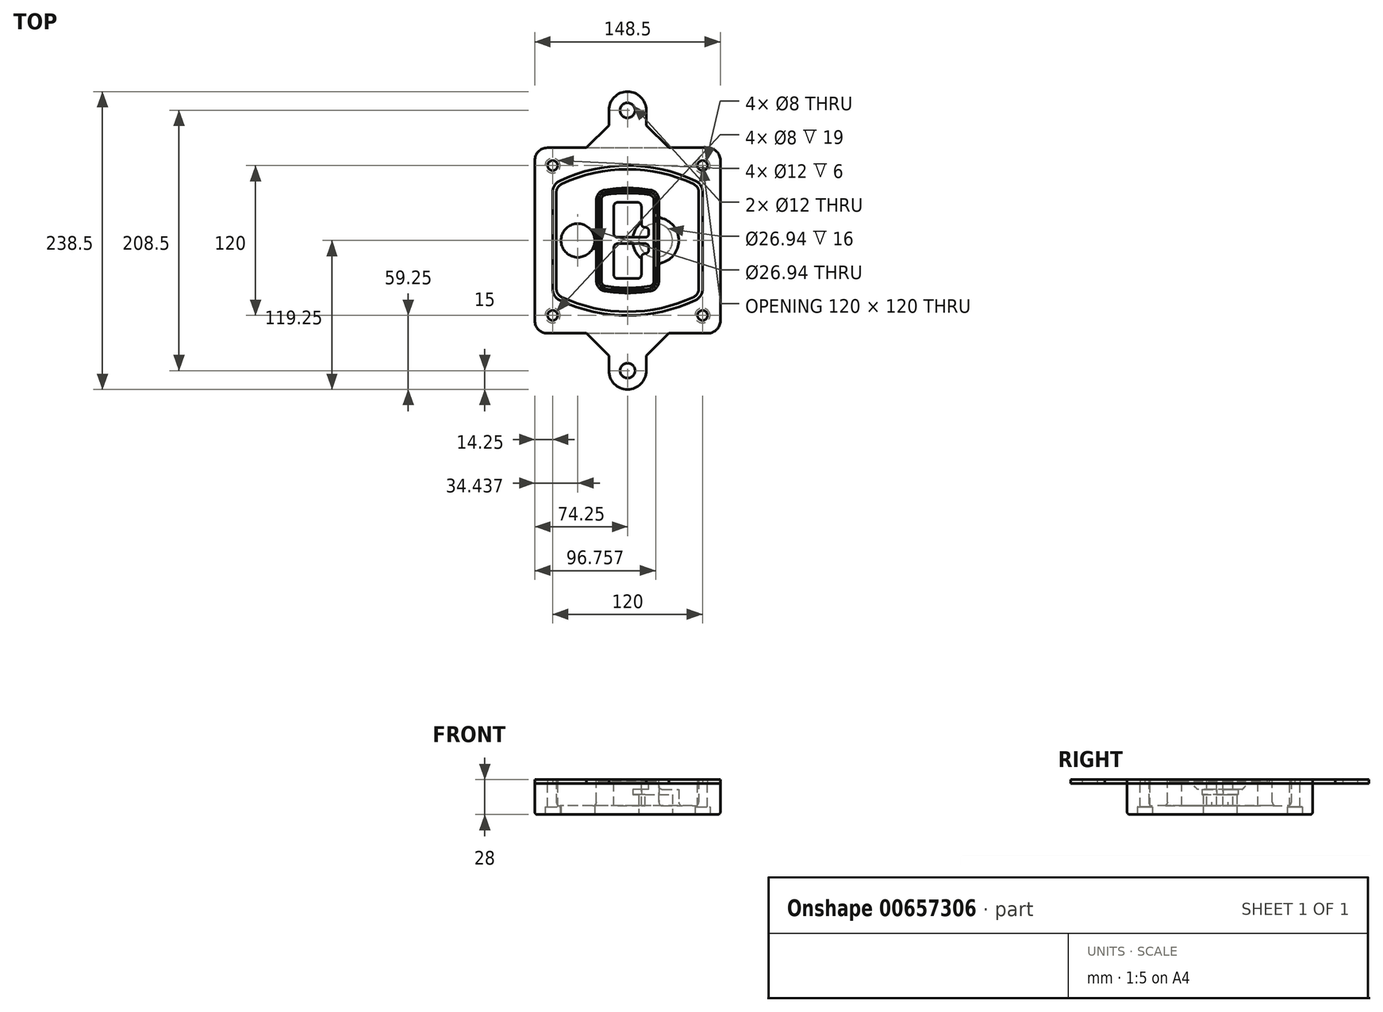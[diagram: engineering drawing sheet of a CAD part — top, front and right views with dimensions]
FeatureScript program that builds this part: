
annotation { "Feature Type Name" : "Feature", "Feature Type Description" : "" }
export const myFeature = defineFeature(function(context is Context, id is Id, definition is map)
    precondition{}
    {
        {
            var Q0;
            Q0=qCreatedBy(makeId("Top.planeOp"),FACE);
            var sketch = newSketch(context, id + "F0", { "sketchPlane" : qUnion([Q0])});
            skPoint(sketch, "E0.rect.middle", {"position": v(0, 0) * mm});
            skLineSegment(sketch, "E1.bottom", {"start": v(-64.25, -74.25) * mm, "end": v(64.25, -74.25) * mm});
            skLineSegment(sketch, "E1.top", {"start": v(-64.25, 74.25) * mm, "end": v(64.25, 74.25) * mm});
            skLineSegment(sketch, "E1.left", {"start": v(-74.25, -64.25) * mm, "end": v(-74.25, 64.25) * mm});
            skLineSegment(sketch, "E1.right", {"start": v(74.25, -64.25) * mm, "end": v(74.25, 64.25) * mm});
            skLineSegment(sketch, "E2", {"start": v(-74.25, 74.25) * mm, "end": v(74.25, -74.25) * mm, "construction": true});
            skLineSegment(sketch, "E3", {"start": v(74.25, 74.25) * mm, "end": v(-74.25, -74.25) * mm, "construction": true});
            skCircle(sketch, "E4", {"center": v(-60, 60) * mm, "radius": 4 * mm});
            skCircle(sketch, "E5", {"center": v(60, 60) * mm, "radius": 4 * mm});
            skCircle(sketch, "E6", {"center": v(60, -60) * mm, "radius": 4 * mm});
            skCircle(sketch, "E7", {"center": v(-60, -60) * mm, "radius": 4 * mm});
            skLineSegment(sketch, "E8", {"start": v(-60, 60) * mm, "end": v(60, 60) * mm, "construction": true});
            skLineSegment(sketch, "E9", {"start": v(60, 60) * mm, "end": v(60, -60) * mm, "construction": true});
            skLineSegment(sketch, "E10", {"start": v(60, -60) * mm, "end": v(-60, -60) * mm, "construction": true});
            skLineSegment(sketch, "E11", {"start": v(-60, -60) * mm, "end": v(-60, 60) * mm, "construction": true});
            skLineSegment(sketch, "E12", {"start": v(-60, 38.83) * mm, "end": v(-60, -38.83) * mm});
            skLineSegment(sketch, "E13", {"start": v(60, 38.83) * mm, "end": v(60, -38.83) * mm});
            skArc(sketch, "E14", {"start": v(54.26, 47.88) * mm, "mid": v(0, 60) * mm, "end": v(-54.26, 47.88) * mm});
            skArc(sketch, "E15", {"start": v(-54.26, -47.88) * mm, "mid": v(0, -60) * mm, "end": v(54.26, -47.88) * mm});
            skLineSegment(sketch, "E16", {"start": v(-60, 0) * mm, "end": v(60, 0) * mm, "construction": true});
            skPoint(sketch, "E17.visualSharp", {"position": v(-60, -45) * mm});
            skArc(sketch, "E17.filletArc", {"start": v(-60, -38.83) * mm, "mid": v(-58.44, -44.2) * mm, "end": v(-54.26, -47.88) * mm});
            skPoint(sketch, "E18.visualSharp", {"position": v(-60, 45) * mm});
            skArc(sketch, "E18.filletArc", {"start": v(-54.26, 47.88) * mm, "mid": v(-58.44, 44.2) * mm, "end": v(-60, 38.83) * mm});
            skPoint(sketch, "E19.visualSharp", {"position": v(60, 45) * mm});
            skArc(sketch, "E19.filletArc", {"start": v(60, 38.83) * mm, "mid": v(58.44, 44.2) * mm, "end": v(54.26, 47.88) * mm});
            skPoint(sketch, "E20.visualSharp", {"position": v(60, -45) * mm});
            skArc(sketch, "E20.filletArc", {"start": v(54.26, -47.88) * mm, "mid": v(58.44, -44.2) * mm, "end": v(60, -38.83) * mm});
            skPoint(sketch, "E21.visualSharp", {"position": v(-74.25, 74.25) * mm});
            skArc(sketch, "E21.filletArc", {"start": v(-64.25, 74.25) * mm, "mid": v(-71.32, 71.32) * mm, "end": v(-74.25, 64.25) * mm});
            skPoint(sketch, "E22.visualSharp", {"position": v(74.25, 74.25) * mm});
            skArc(sketch, "E22.filletArc", {"start": v(74.25, 64.25) * mm, "mid": v(71.32, 71.32) * mm, "end": v(64.25, 74.25) * mm});
            skPoint(sketch, "E23.visualSharp", {"position": v(74.25, -74.25) * mm});
            skArc(sketch, "E23.filletArc", {"start": v(64.25, -74.25) * mm, "mid": v(71.32, -71.32) * mm, "end": v(74.25, -64.25) * mm});
            skPoint(sketch, "E24.visualSharp", {"position": v(-74.25, -74.25) * mm});
            skArc(sketch, "E24.filletArc", {"start": v(-74.25, -64.25) * mm, "mid": v(-71.32, -71.32) * mm, "end": v(-64.25, -74.25) * mm});
            skArc(sketch, "E25.0", {"start": v(57, 38.83) * mm, "mid": v(55.9, 42.58) * mm, "end": v(52.98, 45.17) * mm});
            skLineSegment(sketch, "E25.1", {"start": v(57, 38.83) * mm, "end": v(57, -38.83) * mm});
            skArc(sketch, "E25.2", {"start": v(52.98, -45.17) * mm, "mid": v(55.9, -42.58) * mm, "end": v(57, -38.83) * mm});
            skArc(sketch, "E25.3", {"start": v(-52.98, -45.17) * mm, "mid": v(0, -57) * mm, "end": v(52.98, -45.17) * mm});
            skArc(sketch, "E25.4", {"start": v(-57, -38.83) * mm, "mid": v(-55.9, -42.58) * mm, "end": v(-52.98, -45.17) * mm});
            skArc(sketch, "E25.5", {"start": v(52.98, 45.17) * mm, "mid": v(0, 57) * mm, "end": v(-52.98, 45.17) * mm});
            skLineSegment(sketch, "E25.6", {"start": v(-57, 38.83) * mm, "end": v(-57, -38.83) * mm});
            skArc(sketch, "E25.7", {"start": v(-52.98, 45.17) * mm, "mid": v(-55.9, 42.58) * mm, "end": v(-57, 38.83) * mm});
            skArc(sketch, "E26.0", {"start": v(-55.96, 51.5) * mm, "mid": v(-61.82, 46.33) * mm, "end": v(-64, 38.83) * mm});
            skArc(sketch, "E26.1", {"start": v(55.96, 51.5) * mm, "mid": v(0, 64) * mm, "end": v(-55.96, 51.5) * mm});
            skArc(sketch, "E26.2", {"start": v(64, 38.83) * mm, "mid": v(61.82, 46.33) * mm, "end": v(55.96, 51.5) * mm});
            skLineSegment(sketch, "E26.3", {"start": v(64, 38.83) * mm, "end": v(64, -38.83) * mm});
            skArc(sketch, "E26.4", {"start": v(55.96, -51.5) * mm, "mid": v(61.82, -46.33) * mm, "end": v(64, -38.83) * mm});
            skLineSegment(sketch, "E26.5", {"start": v(-64, 38.83) * mm, "end": v(-64, -38.83) * mm});
            skArc(sketch, "E26.6", {"start": v(-55.96, -51.5) * mm, "mid": v(0, -64) * mm, "end": v(55.96, -51.5) * mm});
            skArc(sketch, "E26.7", {"start": v(-64, -38.83) * mm, "mid": v(-61.82, -46.33) * mm, "end": v(-55.96, -51.5) * mm});
            skLineSegment(sketch, "E27", {"start": v(0, 74.25) * mm, "end": v(0, 104.25) * mm});
            skCircle(sketch, "E28", {"center": v(0, 104.25) * mm, "radius": 6 * mm});
            skArc(sketch, "E29", {"start": v(-15, 104.25) * mm, "mid": v(0, 119.25) * mm, "end": v(15, 104.25) * mm});
            skLineSegment(sketch, "E30", {"start": v(-15, 104.25) * mm, "end": v(-15, 92.25) * mm});
            skLineSegment(sketch, "E31", {"start": v(15, 104.25) * mm, "end": v(15, 92.25) * mm});
            skLineSegment(sketch, "E32", {"start": v(-15, 92.25) * mm, "end": v(-33, 74.25) * mm});
            skLineSegment(sketch, "E33", {"start": v(15, 92.25) * mm, "end": v(33, 74.25) * mm});
            skLineSegment(sketch, "E34", {"start": v(-74.25, 0) * mm, "end": v(74.25, 0) * mm, "construction": true});
            skLineSegment(sketch, "E35", {"start": v(0, -74.25) * mm, "end": v(0, -104.25) * mm});
            skCircle(sketch, "E36", {"center": v(0, -104.25) * mm, "radius": 6 * mm});
            skArc(sketch, "E37", {"start": v(15, -104.25) * mm, "mid": v(0, -119.25) * mm, "end": v(-15, -104.25) * mm});
            skLineSegment(sketch, "E38", {"start": v(15, -104.25) * mm, "end": v(15, -92.25) * mm});
            skLineSegment(sketch, "E39", {"start": v(-15, -104.25) * mm, "end": v(-15, -92.25) * mm});
            skLineSegment(sketch, "E40", {"start": v(-15, -92.25) * mm, "end": v(-33, -74.25) * mm});
            skLineSegment(sketch, "E41", {"start": v(15, -92.25) * mm, "end": v(33, -74.25) * mm});
            skSolve(sketch);
        }
        {
            var Q0;
            Q0=makeQuery(id+"F0.imprint","IMPRINT",FACE,{"disambiguationData":[TD([[makeQuery(id+"F0.imprint","IMPRINT",EDGE,{"derivedFrom":sQuery(id+"F0.wireOp",EDGE,"E1.bottom")}),1.0]])]});
            var Q1;
            Q1=makeQuery(id+"F0.imprint","IMPRINT",FACE,{"disambiguationData":[TD([[makeQuery(id+"F0.imprint","IMPRINT",EDGE,{"derivedFrom":sQuery(id+"F0.wireOp",EDGE,"E12")}),1.0]])]});
            var Q2;
            Q2=makeQuery(id+"F0.imprint","IMPRINT",FACE,{"disambiguationData":[TD([[makeQuery(id+"F0.imprint","IMPRINT",EDGE,{"derivedFrom":sQuery(id+"F0.wireOp",EDGE,"E25.0")}),1.0]])]});
            var Q3;
            Q3=makeQuery(id+"F0.imprint","IMPRINT",FACE,{"disambiguationData":[TD([[makeQuery(id+"F0.imprint","IMPRINT",EDGE,{"derivedFrom":sQuery(id+"F0.wireOp",EDGE,"E12")}),-1.0]])]});
            extrude(context, id + "F1", {"entities" : qUnion([Q0, Q1, Q2, Q3]), "oppositeDirection" : true, "depth" : 25 * mm});
        }
        {
            var Q0;
            Q0=makeQuery(id+"F0.imprint","IMPRINT",FACE,{"disambiguationData":[TD([[makeQuery(id+"F0.imprint","IMPRINT",EDGE,{"derivedFrom":sQuery(id+"F0.wireOp",EDGE,"E12")}),1.0]])]});
            extrude(context, id + "F2", {"entities" : qUnion([Q0]), "operationType" : NewBodyOperationType.ADD, "depth" : 3 * mm});
        }
        {
            var Q0;
            Q0=makeQuery(id+"F0.imprint","IMPRINT",FACE,{"disambiguationData":[TD([[makeQuery(id+"F0.imprint","IMPRINT",EDGE,{"derivedFrom":sQuery(id+"F0.wireOp",EDGE,"E25.0")}),1.0]])]});
            extrude(context, id + "F3", {"entities" : qUnion([Q0]), "operationType" : NewBodyOperationType.REMOVE, "oppositeDirection" : true, "depth" : 18 * mm});
        }
        {
            var Q0;
            Q0=makeQuery(id+"F2.opExtrude","CAP_FACE",FACE,{"disambiguationData":[OSD([sQuery(id+"F0.wireOp",EDGE,"E12"),sQuery(id+"F0.wireOp",EDGE,"E13"),sQuery(id+"F0.wireOp",EDGE,"E14"),sQuery(id+"F0.wireOp",EDGE,"E15"),sQuery(id+"F0.wireOp",EDGE,"E17.filletArc"),sQuery(id+"F0.wireOp",EDGE,"E18.filletArc"),sQuery(id+"F0.wireOp",EDGE,"E19.filletArc"),sQuery(id+"F0.wireOp",EDGE,"E20.filletArc"),sQuery(id+"F0.wireOp",EDGE,"E25.0"),sQuery(id+"F0.wireOp",EDGE,"E25.1"),sQuery(id+"F0.wireOp",EDGE,"E25.2"),sQuery(id+"F0.wireOp",EDGE,"E25.3"),sQuery(id+"F0.wireOp",EDGE,"E25.4"),sQuery(id+"F0.wireOp",EDGE,"E25.5"),sQuery(id+"F0.wireOp",EDGE,"E25.6"),sQuery(id+"F0.wireOp",EDGE,"E25.7")])],"isStart":false});
            var sketch = newSketch(context, id + "F4", { "sketchPlane" : qUnion([Q0])});
            skArc(sketch, "E42.0", {"start": v(-18.34, -40.45) * mm, "mid": v(0, -42) * mm, "end": v(18.34, -40.45) * mm});
            skArc(sketch, "E43.0", {"start": v(18.34, 40.45) * mm, "mid": v(0, 42) * mm, "end": v(-18.34, 40.45) * mm});
            skLineSegment(sketch, "E44", {"start": v(-25, 32.57) * mm, "end": v(-25, -32.57) * mm});
            skLineSegment(sketch, "E45", {"start": v(25, 32.57) * mm, "end": v(25, -32.57) * mm});
            skLineSegment(sketch, "E46", {"start": v(-25, 39.1) * mm, "end": v(25, 39.1) * mm, "construction": true});
            skLineSegment(sketch, "E47", {"start": v(-25, -39.1) * mm, "end": v(25, -39.1) * mm, "construction": true});
            skPoint(sketch, "E48.visualSharp", {"position": v(-25, 39.1) * mm});
            skArc(sketch, "E48.filletArc", {"start": v(-18.34, 40.45) * mm, "mid": v(-23.11, 37.73) * mm, "end": v(-25, 32.57) * mm});
            skPoint(sketch, "E49.visualSharp", {"position": v(25, 39.1) * mm});
            skArc(sketch, "E49.filletArc", {"start": v(25, 32.57) * mm, "mid": v(23.11, 37.73) * mm, "end": v(18.34, 40.45) * mm});
            skPoint(sketch, "E50.visualSharp", {"position": v(25, -39.1) * mm});
            skArc(sketch, "E50.filletArc", {"start": v(18.34, -40.45) * mm, "mid": v(23.11, -37.73) * mm, "end": v(25, -32.57) * mm});
            skPoint(sketch, "E51.visualSharp", {"position": v(-25, -39.1) * mm});
            skArc(sketch, "E51.filletArc", {"start": v(-25, -32.57) * mm, "mid": v(-23.11, -37.73) * mm, "end": v(-18.34, -40.45) * mm});
            skArc(sketch, "E52.0", {"start": v(52.98, 45.17) * mm, "mid": v(0, 57) * mm, "end": v(-52.98, 45.17) * mm});
            skArc(sketch, "E52.1", {"start": v(-52.98, 45.17) * mm, "mid": v(-55.9, 42.58) * mm, "end": v(-57, 38.83) * mm});
            skLineSegment(sketch, "E52.2", {"start": v(-57, 38.83) * mm, "end": v(-57, -38.83) * mm});
            skArc(sketch, "E52.3", {"start": v(-57, -38.83) * mm, "mid": v(-55.9, -42.58) * mm, "end": v(-52.98, -45.17) * mm});
            skArc(sketch, "E52.4", {"start": v(-52.98, -45.17) * mm, "mid": v(0, -57) * mm, "end": v(52.98, -45.17) * mm});
            skArc(sketch, "E52.5", {"start": v(52.98, -45.17) * mm, "mid": v(55.9, -42.58) * mm, "end": v(57, -38.83) * mm});
            skLineSegment(sketch, "E52.6", {"start": v(57, 38.83) * mm, "end": v(57, -38.83) * mm});
            skArc(sketch, "E52.7", {"start": v(57, 38.83) * mm, "mid": v(55.9, 42.58) * mm, "end": v(52.98, 45.17) * mm});
            skLineSegment(sketch, "E53.0", {"start": v(23, 32.57) * mm, "end": v(23, -32.57) * mm});
            skArc(sketch, "E53.1", {"start": v(18, -38.48) * mm, "mid": v(21.58, -36.44) * mm, "end": v(23, -32.57) * mm});
            skArc(sketch, "E53.2", {"start": v(-18, -38.48) * mm, "mid": v(0, -40) * mm, "end": v(18, -38.48) * mm});
            skArc(sketch, "E53.3", {"start": v(-23, -32.57) * mm, "mid": v(-21.58, -36.44) * mm, "end": v(-18, -38.48) * mm});
            skLineSegment(sketch, "E53.4", {"start": v(-23, 32.57) * mm, "end": v(-23, -32.57) * mm});
            skArc(sketch, "E53.5", {"start": v(23, 32.57) * mm, "mid": v(21.58, 36.44) * mm, "end": v(18, 38.48) * mm});
            skArc(sketch, "E53.6", {"start": v(-18, 38.48) * mm, "mid": v(-21.58, 36.44) * mm, "end": v(-23, 32.57) * mm});
            skArc(sketch, "E53.7", {"start": v(18, 38.48) * mm, "mid": v(0, 40) * mm, "end": v(-18, 38.48) * mm});
            skArc(sketch, "E54.0", {"start": v(21, 32.57) * mm, "mid": v(20.06, 35.15) * mm, "end": v(17.67, 36.5) * mm});
            skLineSegment(sketch, "E54.1", {"start": v(21, 32.57) * mm, "end": v(21, -32.57) * mm});
            skArc(sketch, "E54.2", {"start": v(17.67, -36.5) * mm, "mid": v(20.06, -35.15) * mm, "end": v(21, -32.57) * mm});
            skArc(sketch, "E54.3", {"start": v(-17.67, -36.5) * mm, "mid": v(0, -38) * mm, "end": v(17.67, -36.5) * mm});
            skArc(sketch, "E54.4", {"start": v(-21, -32.57) * mm, "mid": v(-20.06, -35.15) * mm, "end": v(-17.67, -36.5) * mm});
            skArc(sketch, "E54.5", {"start": v(17.67, 36.5) * mm, "mid": v(0, 38) * mm, "end": v(-17.67, 36.5) * mm});
            skLineSegment(sketch, "E54.6", {"start": v(-21, 32.57) * mm, "end": v(-21, -32.57) * mm});
            skArc(sketch, "E54.7", {"start": v(-17.67, 36.5) * mm, "mid": v(-20.06, 35.15) * mm, "end": v(-21, 32.57) * mm});
            skLineSegment(sketch, "E55", {"start": v(-25, 0) * mm, "end": v(25, 0) * mm, "construction": true});
            skLineSegment(sketch, "E56", {"start": v(-11, 5.5) * mm, "end": v(-11, 27.5) * mm});
            skLineSegment(sketch, "E57", {"start": v(-8, 30.5) * mm, "end": v(8, 30.5) * mm});
            skLineSegment(sketch, "E58", {"start": v(11, 27.5) * mm, "end": v(11, 13.5) * mm});
            skLineSegment(sketch, "E59", {"start": v(14, 10.5) * mm, "end": v(14, 10.5) * mm});
            skLineSegment(sketch, "E60", {"start": v(17, 7.5) * mm, "end": v(17, 5.5) * mm});
            skLineSegment(sketch, "E61", {"start": v(14, 2.5) * mm, "end": v(-8, 2.5) * mm});
            skPoint(sketch, "E62.visualSharp", {"position": v(-11, 30.5) * mm});
            skArc(sketch, "E62.filletArc", {"start": v(-8, 30.5) * mm, "mid": v(-10.12, 29.62) * mm, "end": v(-11, 27.5) * mm});
            skPoint(sketch, "E63.visualSharp", {"position": v(11, 30.5) * mm});
            skArc(sketch, "E63.filletArc", {"start": v(11, 27.5) * mm, "mid": v(10.12, 29.62) * mm, "end": v(8, 30.5) * mm});
            skPoint(sketch, "E64.visualSharp", {"position": v(11, 10.5) * mm});
            skArc(sketch, "E64.filletArc", {"start": v(11, 13.5) * mm, "mid": v(11.88, 11.38) * mm, "end": v(14, 10.5) * mm});
            skPoint(sketch, "E65.visualSharp", {"position": v(17, 10.5) * mm});
            skArc(sketch, "E65.filletArc", {"start": v(17, 7.5) * mm, "mid": v(16.12, 9.62) * mm, "end": v(14, 10.5) * mm});
            skPoint(sketch, "E66.visualSharp", {"position": v(17, 2.5) * mm});
            skArc(sketch, "E66.filletArc", {"start": v(14, 2.5) * mm, "mid": v(16.12, 3.38) * mm, "end": v(17, 5.5) * mm});
            skPoint(sketch, "E67.visualSharp", {"position": v(-11, 2.5) * mm});
            skArc(sketch, "E67.filletArc", {"start": v(-11, 5.5) * mm, "mid": v(-10.12, 3.38) * mm, "end": v(-8, 2.5) * mm});
            skLineSegment(sketch, "E68.0.MirrorCS", {"start": v(14, -2.5) * mm, "end": v(-8, -2.5) * mm});
            skArc(sketch, "E69.0.MirrorCS", {"start": v(-11, -5.5) * mm, "mid": v(-10.12, -3.38) * mm, "end": v(-8, -2.5) * mm});
            skLineSegment(sketch, "E70.0.MirrorCS", {"start": v(-11, -5.5) * mm, "end": v(-11, -27.5) * mm});
            skArc(sketch, "E71.0.MirrorCS", {"start": v(-8, -30.5) * mm, "mid": v(-10.12, -29.62) * mm, "end": v(-11, -27.5) * mm});
            skLineSegment(sketch, "E72.0.MirrorCS", {"start": v(-8, -30.5) * mm, "end": v(8, -30.5) * mm});
            skArc(sketch, "E73.0.MirrorCS", {"start": v(11, -27.5) * mm, "mid": v(10.12, -29.62) * mm, "end": v(8, -30.5) * mm});
            skLineSegment(sketch, "E74.0.MirrorCS", {"start": v(11, -27.5) * mm, "end": v(11, -13.5) * mm});
            skArc(sketch, "E75.0.MirrorCS", {"start": v(11, -13.5) * mm, "mid": v(11.88, -11.38) * mm, "end": v(14, -10.5) * mm});
            skArc(sketch, "E76.0.MirrorCS", {"start": v(17, -7.5) * mm, "mid": v(16.12, -9.62) * mm, "end": v(14, -10.5) * mm});
            skLineSegment(sketch, "E77.0.MirrorCS", {"start": v(17, -7.5) * mm, "end": v(17, -5.5) * mm});
            skArc(sketch, "E78.0.MirrorCS", {"start": v(14, -2.5) * mm, "mid": v(16.12, -3.38) * mm, "end": v(17, -5.5) * mm});
            skSolve(sketch);
        }
        {
            var Q0;
            Q0=makeQuery(id+"F4.imprint","IMPRINT",FACE,{"disambiguationData":[TD([[makeQuery(id+"F4.imprint","IMPRINT",EDGE,{"derivedFrom":sQuery(id+"F4.wireOp",EDGE,"E42.0")}),1.0]])]});
            var Q1;
            Q1=makeQuery(id+"F4.imprint","IMPRINT",FACE,{"disambiguationData":[TD([[makeQuery(id+"F4.imprint","IMPRINT",EDGE,{"derivedFrom":sQuery(id+"F4.wireOp",EDGE,"E53.0")}),-1.0]])]});
            var Q2;
            Q2=makeQuery(id+"F4.imprint","IMPRINT",FACE,{"disambiguationData":[TD([[makeQuery(id+"F4.imprint","IMPRINT",EDGE,{"derivedFrom":sQuery(id+"F4.wireOp",EDGE,"E54.0")}),1.0]])]});
            extrude(context, id + "F5", {"entities" : qUnion([Q0, Q1, Q2]), "operationType" : NewBodyOperationType.ADD, "endBound" : BoundingType.UP_TO_NEXT, "oppositeDirection" : true, "depth" : 25 * mm});
        }
        {
            var Q0;
            Q0=makeQuery(id+"F4.imprint","IMPRINT",FACE,{"disambiguationData":[TD([[makeQuery(id+"F4.imprint","IMPRINT",EDGE,{"derivedFrom":sQuery(id+"F4.wireOp",EDGE,"E53.0")}),-1.0]])]});
            extrude(context, id + "F6", {"entities" : qUnion([Q0]), "operationType" : NewBodyOperationType.REMOVE, "oppositeDirection" : true, "depth" : 2 * mm});
        }
        {
            var Q0;
            Q0=makeQuery(id+"F1.opExtrude","CAP_FACE",FACE,{"disambiguationData":[OSD([sQuery(id+"F0.wireOp",EDGE,"E1.bottom"),sQuery(id+"F0.wireOp",EDGE,"E1.top"),sQuery(id+"F0.wireOp",EDGE,"E1.left"),sQuery(id+"F0.wireOp",EDGE,"E1.right"),sQuery(id+"F0.wireOp",EDGE,"E4"),sQuery(id+"F0.wireOp",EDGE,"E5"),sQuery(id+"F0.wireOp",EDGE,"E6"),sQuery(id+"F0.wireOp",EDGE,"E7"),sQuery(id+"F0.wireOp",EDGE,"E21.filletArc"),sQuery(id+"F0.wireOp",EDGE,"E22.filletArc"),sQuery(id+"F0.wireOp",EDGE,"E23.filletArc"),sQuery(id+"F0.wireOp",EDGE,"E24.filletArc")])],"isStart":false});
            var sketch = newSketch(context, id + "F7", { "sketchPlane" : qUnion([Q0])});
            skCircle(sketch, "E79", {"center": v(22.5, 0) * mm, "radius": 13.47 * mm});
            skCircle(sketch, "E80", {"center": v(-39.81, 0) * mm, "radius": 13.47 * mm});
            skLineSegment(sketch, "E81", {"start": v(74.25, 0) * mm, "end": v(-74.25, 0) * mm});
            skCircle(sketch, "E82", {"center": v(22.5, 0) * mm, "radius": 18.47 * mm});
            skCircle(sketch, "E83", {"center": v(60, -60) * mm, "radius": 6 * mm});
            skCircle(sketch, "E84", {"center": v(-60, -60) * mm, "radius": 6 * mm});
            skCircle(sketch, "E85", {"center": v(-60, 60) * mm, "radius": 6 * mm});
            skCircle(sketch, "E86", {"center": v(60, 60) * mm, "radius": 6 * mm});
            skSolve(sketch);
        }
        {
            var Q0;
            {var subQ1=sQuery(id+"F7.wireOp",EDGE,"E81");var subQ4=sQuery(id+"F7.wireOp",EDGE,"E79");var subQ6=makeQuery(id+"F7.imprint","INTERSECT",VERTEX,{"disambiguationData":[OD(0.0)],"derivedFrom":[subQ4,subQ1]});Q0=makeQuery(id+"F7.imprint","IMPRINT",FACE,{"disambiguationData":[TD([[makeQuery(id+"F7.imprint","IMPRINT",EDGE,{"disambiguationData":[TD([[subQ6,-1.0]])],"derivedFrom":subQ4}),-1.0]])]});}
            var Q1;
            {var subQ0=sQuery(id+"F7.wireOp",EDGE,"E81");var subQ1=sQuery(id+"F7.wireOp",EDGE,"E79");var subQ3=makeQuery(id+"F7.imprint","INTERSECT",VERTEX,{"disambiguationData":[OD(0.0)],"derivedFrom":[subQ1,subQ0]});Q1=makeQuery(id+"F7.imprint","IMPRINT",FACE,{"disambiguationData":[TD([[makeQuery(id+"F7.imprint","IMPRINT",EDGE,{"disambiguationData":[TD([[subQ3,-1.0]])],"derivedFrom":subQ1}),1.0]])]});}
            var Q2;
            {var subQ0=sQuery(id+"F7.wireOp",EDGE,"E81");var subQ1=sQuery(id+"F7.wireOp",EDGE,"E79");var subQ3=makeQuery(id+"F7.imprint","INTERSECT",VERTEX,{"disambiguationData":[OD(0.0)],"derivedFrom":[subQ1,subQ0]});Q2=makeQuery(id+"F7.imprint","IMPRINT",FACE,{"disambiguationData":[TD([[makeQuery(id+"F7.imprint","IMPRINT",EDGE,{"disambiguationData":[TD([[subQ3,1.0]])],"derivedFrom":subQ1}),1.0]])]});}
            var Q3;
            {var subQ1=sQuery(id+"F7.wireOp",EDGE,"E81");var subQ4=sQuery(id+"F7.wireOp",EDGE,"E79");var subQ6=makeQuery(id+"F7.imprint","INTERSECT",VERTEX,{"disambiguationData":[OD(0.0)],"derivedFrom":[subQ4,subQ1]});Q3=makeQuery(id+"F7.imprint","IMPRINT",FACE,{"disambiguationData":[TD([[makeQuery(id+"F7.imprint","IMPRINT",EDGE,{"disambiguationData":[TD([[subQ6,1.0]])],"derivedFrom":subQ4}),-1.0]])]});}
            extrude(context, id + "F8", {"entities" : qUnion([Q0, Q1, Q2, Q3]), "operationType" : NewBodyOperationType.ADD, "oppositeDirection" : true, "depth" : 20 * mm});
        }
        {
            var Q0;
            {var subQ0=sQuery(id+"F7.wireOp",EDGE,"E81");var subQ1=sQuery(id+"F7.wireOp",EDGE,"E79");var subQ3=makeQuery(id+"F7.imprint","INTERSECT",VERTEX,{"disambiguationData":[OD(0.0)],"derivedFrom":[subQ1,subQ0]});Q0=makeQuery(id+"F7.imprint","IMPRINT",FACE,{"disambiguationData":[TD([[makeQuery(id+"F7.imprint","IMPRINT",EDGE,{"disambiguationData":[TD([[subQ3,-1.0]])],"derivedFrom":subQ1}),1.0]])]});}
            var Q1;
            {var subQ0=sQuery(id+"F7.wireOp",EDGE,"E81");var subQ1=sQuery(id+"F7.wireOp",EDGE,"E79");var subQ3=makeQuery(id+"F7.imprint","INTERSECT",VERTEX,{"disambiguationData":[OD(0.0)],"derivedFrom":[subQ1,subQ0]});Q1=makeQuery(id+"F7.imprint","IMPRINT",FACE,{"disambiguationData":[TD([[makeQuery(id+"F7.imprint","IMPRINT",EDGE,{"disambiguationData":[TD([[subQ3,1.0]])],"derivedFrom":subQ1}),1.0]])]});}
            extrude(context, id + "F9", {"entities" : qUnion([Q0, Q1]), "operationType" : NewBodyOperationType.REMOVE, "oppositeDirection" : true, "depth" : 16 * mm});
        }
        {
            var Q0;
            {var subQ0=sQuery(id+"F7.wireOp",EDGE,"E81");var subQ1=sQuery(id+"F7.wireOp",EDGE,"E80");var subQ3=makeQuery(id+"F7.imprint","INTERSECT",VERTEX,{"disambiguationData":[OD(0.0)],"derivedFrom":[subQ1,subQ0]});Q0=makeQuery(id+"F7.imprint","IMPRINT",FACE,{"disambiguationData":[TD([[makeQuery(id+"F7.imprint","IMPRINT",EDGE,{"disambiguationData":[TD([[subQ3,-1.0]])],"derivedFrom":subQ1}),1.0]])]});}
            var Q1;
            {var subQ0=sQuery(id+"F7.wireOp",EDGE,"E81");var subQ1=sQuery(id+"F7.wireOp",EDGE,"E80");var subQ3=makeQuery(id+"F7.imprint","INTERSECT",VERTEX,{"disambiguationData":[OD(0.0)],"derivedFrom":[subQ1,subQ0]});Q1=makeQuery(id+"F7.imprint","IMPRINT",FACE,{"disambiguationData":[TD([[makeQuery(id+"F7.imprint","IMPRINT",EDGE,{"disambiguationData":[TD([[subQ3,1.0]])],"derivedFrom":subQ1}),1.0]])]});}
            extrude(context, id + "F10", {"entities" : qUnion([Q0, Q1]), "operationType" : NewBodyOperationType.REMOVE, "oppositeDirection" : true, "depth" : 25 * mm});
        }
        {
            var Q0;
            Q0=makeQuery(id+"F7.imprint","IMPRINT",FACE,{"disambiguationData":[TD([[makeQuery(id+"F7.imprint","IMPRINT",EDGE,{"derivedFrom":sQuery(id+"F7.wireOp",EDGE,"E83")}),1.0]])]});
            var Q1;
            Q1=makeQuery(id+"F7.imprint","IMPRINT",FACE,{"disambiguationData":[TD([[makeQuery(id+"F7.imprint","IMPRINT",EDGE,{"derivedFrom":makeQuery(id+"F1.opExtrude","CAP_EDGE",EDGE,{"disambiguationData":[OSD([sQuery(id+"F0.wireOp",EDGE,"E5")])],"isStart":false})}),-1.0]])]});
            var Q2;
            Q2=makeQuery(id+"F7.imprint","IMPRINT",FACE,{"disambiguationData":[TD([[makeQuery(id+"F7.imprint","IMPRINT",EDGE,{"derivedFrom":sQuery(id+"F7.wireOp",EDGE,"E84")}),1.0]])]});
            var Q3;
            Q3=makeQuery(id+"F7.imprint","IMPRINT",FACE,{"disambiguationData":[TD([[makeQuery(id+"F7.imprint","IMPRINT",EDGE,{"derivedFrom":makeQuery(id+"F1.opExtrude","CAP_EDGE",EDGE,{"disambiguationData":[OSD([sQuery(id+"F0.wireOp",EDGE,"E4")])],"isStart":false})}),-1.0]])]});
            var Q4;
            Q4=makeQuery(id+"F7.imprint","IMPRINT",FACE,{"disambiguationData":[TD([[makeQuery(id+"F7.imprint","IMPRINT",EDGE,{"derivedFrom":sQuery(id+"F7.wireOp",EDGE,"E85")}),1.0]])]});
            var Q5;
            Q5=makeQuery(id+"F7.imprint","IMPRINT",FACE,{"disambiguationData":[TD([[makeQuery(id+"F7.imprint","IMPRINT",EDGE,{"derivedFrom":makeQuery(id+"F1.opExtrude","CAP_EDGE",EDGE,{"disambiguationData":[OSD([sQuery(id+"F0.wireOp",EDGE,"E7")])],"isStart":false})}),-1.0]])]});
            var Q6;
            Q6=makeQuery(id+"F7.imprint","IMPRINT",FACE,{"disambiguationData":[TD([[makeQuery(id+"F7.imprint","IMPRINT",EDGE,{"derivedFrom":sQuery(id+"F7.wireOp",EDGE,"E86")}),1.0]])]});
            var Q7;
            Q7=makeQuery(id+"F7.imprint","IMPRINT",FACE,{"disambiguationData":[TD([[makeQuery(id+"F7.imprint","IMPRINT",EDGE,{"derivedFrom":makeQuery(id+"F1.opExtrude","CAP_EDGE",EDGE,{"disambiguationData":[OSD([sQuery(id+"F0.wireOp",EDGE,"E6")])],"isStart":false})}),-1.0]])]});
            extrude(context, id + "F11", {"entities" : qUnion([Q0, Q1, Q2, Q3, Q4, Q5, Q6, Q7]), "operationType" : NewBodyOperationType.REMOVE, "oppositeDirection" : true, "depth" : 6 * mm});
        }
        {
            var Q0;
            Q0=makeQuery(id+"F9.boolean.opBoolean","COPY",FACE,{"derivedFrom":makeQuery(id+"F9.opExtrude","CAP_FACE",FACE,{"disambiguationData":[OSD([sQuery(id+"F7.wireOp",EDGE,"E79")])],"isStart":false})});
            var sketch = newSketch(context, id + "F12", { "sketchPlane" : qUnion([Q0])});
            skArc(sketch, "E87.0", {"start": v(11, 14.45) * mm, "mid": v(6.45, 9.13) * mm, "end": v(4.2, 2.5) * mm});
            skArc(sketch, "E87.1", {"start": v(4.2, -2.5) * mm, "mid": v(6.45, -9.13) * mm, "end": v(11, -14.45) * mm});
            skLineSegment(sketch, "E88", {"start": v(4.2, -2.5) * mm, "end": v(14, -2.5) * mm});
            skLineSegment(sketch, "E89.0", {"start": v(14, 2.5) * mm, "end": v(4.2, 2.5) * mm});
            skArc(sketch, "E89.1", {"start": v(14, 2.5) * mm, "mid": v(16.12, 3.38) * mm, "end": v(17, 5.5) * mm});
            skLineSegment(sketch, "E89.2", {"start": v(17, 7.5) * mm, "end": v(17, 5.5) * mm});
            skArc(sketch, "E89.3", {"start": v(17, 7.5) * mm, "mid": v(16.12, 9.62) * mm, "end": v(14, 10.5) * mm});
            skArc(sketch, "E89.4", {"start": v(11, 13.5) * mm, "mid": v(11.88, 11.38) * mm, "end": v(14, 10.5) * mm});
            skLineSegment(sketch, "E89.5", {"start": v(11, 14.45) * mm, "end": v(11, 13.5) * mm});
            skLineSegment(sketch, "E89.7", {"start": v(14, -2.5) * mm, "end": v(4.2, -2.5) * mm});
            skArc(sketch, "E89.8", {"start": v(14, -2.5) * mm, "mid": v(16.12, -3.38) * mm, "end": v(17, -5.5) * mm});
            skLineSegment(sketch, "E89.9", {"start": v(17, -7.5) * mm, "end": v(17, -5.5) * mm});
            skArc(sketch, "E89.10", {"start": v(17, -7.5) * mm, "mid": v(16.12, -9.62) * mm, "end": v(14, -10.5) * mm});
            skArc(sketch, "E89.11", {"start": v(11, -13.5) * mm, "mid": v(11.88, -11.38) * mm, "end": v(14, -10.5) * mm});
            skLineSegment(sketch, "E89.12", {"start": v(11, -14.45) * mm, "end": v(11, -13.5) * mm});
            skPoint(sketch, "E90.orphan", {"position": v(11, -27.5) * mm});
            skPoint(sketch, "E91.orphan", {"position": v(-8, -2.5) * mm});
            skPoint(sketch, "E92.orphan", {"position": v(-8, 2.5) * mm});
            skPoint(sketch, "E93.orphan", {"position": v(11, 27.5) * mm});
            skSolve(sketch);
        }
        {
            var Q0;
            {var subQ7=sQuery(id+"F12.wireOp",EDGE,"E87.0");var subQ14=sQuery(id+"F12.wireOp",EDGE,"E87.1");var subQ16=sQuery(id+"F12.wireOp",EDGE,"E89.1");var subQ18=sQuery(id+"F12.wireOp",EDGE,"E89.8");Q0=qUnion([makeQuery(id+"F12.imprint","IMPRINT",FACE,{"disambiguationData":[TD([[makeQuery(id+"F12.imprint","IMPRINT",EDGE,{"derivedFrom":subQ7}),1.0]])]}),makeQuery(id+"F12.imprint","IMPRINT",FACE,{"disambiguationData":[TD([[makeQuery(id+"F12.imprint","IMPRINT",EDGE,{"derivedFrom":subQ14}),1.0]])]}),makeQuery(id+"F12.imprint","IMPRINT",FACE,{"disambiguationData":[TD([[makeQuery(id+"F12.imprint","IMPRINT",EDGE,{"derivedFrom":subQ16}),1.0]])]}),makeQuery(id+"F12.imprint","IMPRINT",FACE,{"disambiguationData":[TD([[makeQuery(id+"F12.imprint","IMPRINT",EDGE,{"derivedFrom":subQ18}),-1.0]])]})]);}
            var Q1;
            Q1=makeQuery(id+"F5.boolean.opBoolean","SPLIT",FACE,{"disambiguationData":[TD([makeQuery(id+"F5.opExtrude","SWEPT_FACE",FACE,{"disambiguationData":[OSD([sQuery(id+"F4.wireOp",EDGE,"E56")])]})])],"derivedFrom":makeQuery(id+"F3.boolean.opBoolean","COPY",FACE,{"derivedFrom":makeQuery(id+"F3.opExtrude","CAP_FACE",FACE,{"disambiguationData":[OSD([sQuery(id+"F0.wireOp",EDGE,"E25.0"),sQuery(id+"F0.wireOp",EDGE,"E25.1"),sQuery(id+"F0.wireOp",EDGE,"E25.2"),sQuery(id+"F0.wireOp",EDGE,"E25.3"),sQuery(id+"F0.wireOp",EDGE,"E25.4"),sQuery(id+"F0.wireOp",EDGE,"E25.5"),sQuery(id+"F0.wireOp",EDGE,"E25.6"),sQuery(id+"F0.wireOp",EDGE,"E25.7")])],"isStart":false})})});
            extrude(context, id + "F13", {"entities" : qUnion([Q0]), "operationType" : NewBodyOperationType.REMOVE, "endBound" : BoundingType.UP_TO_SURFACE, "endBoundEntityFace" : qUnion([Q1]), "depth" : 25 * mm});
        }
        {
            var Q0;
            Q0=makeQuery(id+"F3.boolean.opBoolean","COPY",EDGE,{"derivedFrom":makeQuery(id+"F3.opExtrude","CAP_EDGE",EDGE,{"disambiguationData":[OSD([sQuery(id+"F0.wireOp",EDGE,"E25.6")])],"isStart":false})});
            var Q1;
            Q1=makeQuery(id+"F8.boolean.opBoolean","INTERSECT",EDGE,{"derivedFrom":[makeQuery(id+"F5.opExtrude","SWEPT_FACE",FACE,{"disambiguationData":[OSD([sQuery(id+"F4.wireOp",EDGE,"E45")])]}),makeQuery(id+"F8.opExtrude","CAP_FACE",FACE,{"disambiguationData":[OSD([sQuery(id+"F7.wireOp",EDGE,"E82")])],"isStart":false})]});
            var Q2;
            Q2=makeQuery(id+"F8.boolean.opBoolean","INTERSECT",EDGE,{"disambiguationData":[OD(1.0)],"derivedFrom":[makeQuery(id+"F5.opExtrude","SWEPT_FACE",FACE,{"disambiguationData":[OSD([sQuery(id+"F4.wireOp",EDGE,"E45")])]}),makeQuery(id+"F8.opExtrude","SWEPT_FACE",FACE,{"disambiguationData":[OSD([sQuery(id+"F7.wireOp",EDGE,"E82")])]})]});
            var Q3;
            {var subQ0=sQuery(id+"F4.wireOp",EDGE,"E45");Q3=makeQuery(id+"F8.boolean.opBoolean","SPLIT",EDGE,{"disambiguationData":[TD([makeQuery(id+"F5.opExtrude","SWEPT_FACE",FACE,{"disambiguationData":[OSD([sQuery(id+"F4.wireOp",EDGE,"E50.filletArc")])]})])],"derivedFrom":makeQuery(id+"F5.opExtrude","CAP_EDGE",EDGE,{"disambiguationData":[OSD([subQ0])],"isStart":false})});}
            var Q4;
            {var subQ0=sQuery(id+"F0.wireOp",EDGE,"E25.7");var subQ1=sQuery(id+"F0.wireOp",EDGE,"E25.1");var subQ2=sQuery(id+"F0.wireOp",EDGE,"E25.6");var subQ3=sQuery(id+"F0.wireOp",EDGE,"E25.5");var subQ4=sQuery(id+"F0.wireOp",EDGE,"E25.4");var subQ5=sQuery(id+"F0.wireOp",EDGE,"E25.0");var subQ6=sQuery(id+"F0.wireOp",EDGE,"E25.2");var subQ7=sQuery(id+"F0.wireOp",EDGE,"E25.3");Q4=makeQuery(id+"F8.boolean.opBoolean","INTERSECT",EDGE,{"derivedFrom":[makeQuery(id+"F5.boolean.opBoolean","SPLIT",FACE,{"disambiguationData":[TD([makeQuery(id+"F2.opExtrude","SWEPT_FACE",FACE,{"disambiguationData":[OSD([subQ5])]})])],"derivedFrom":makeQuery(id+"F3.boolean.opBoolean","COPY",FACE,{"derivedFrom":makeQuery(id+"F3.opExtrude","CAP_FACE",FACE,{"disambiguationData":[OSD([subQ5,subQ1,subQ6,subQ7,subQ4,subQ3,subQ2,subQ0])],"isStart":false})})}),makeQuery(id+"F8.opExtrude","SWEPT_FACE",FACE,{"disambiguationData":[OSD([sQuery(id+"F7.wireOp",EDGE,"E82")])]})]});}
            var Q5;
            Q5=makeQuery(id+"F8.boolean.opBoolean","INTERSECT",EDGE,{"disambiguationData":[OD(0.0)],"derivedFrom":[makeQuery(id+"F5.opExtrude","SWEPT_FACE",FACE,{"disambiguationData":[OSD([sQuery(id+"F4.wireOp",EDGE,"E45")])]}),makeQuery(id+"F8.opExtrude","SWEPT_FACE",FACE,{"disambiguationData":[OSD([sQuery(id+"F7.wireOp",EDGE,"E82")])]})]});
            fillet(context, id + "F14", {"entities" : qUnion([Q0, Q1, Q2, Q3, Q4, Q5]), "radius" : 3 * mm, "tangentPropagation" : true, "allowEdgeOverflow" : false});
        }
        {
            var Q0;
            Q0=makeQuery(id+"F1.opExtrude","CAP_EDGE",EDGE,{"disambiguationData":[OSD([sQuery(id+"F0.wireOp",EDGE,"E1.bottom")])],"isStart":false});
            fillet(context, id + "F15", {"entities" : qUnion([Q0]), "radius" : 2 * mm, "tangentPropagation" : true, "allowEdgeOverflow" : false});
        }
        {
            var Q0;
            Q0=makeQuery(id+"F0.imprint","IMPRINT",FACE,{"disambiguationData":[TD([[makeQuery(id+"F0.imprint","IMPRINT",EDGE,{"derivedFrom":sQuery(id+"F0.wireOp",EDGE,"E36")}),-1.0]])]});
            var Q1;
            Q1=makeQuery(id+"F0.imprint","IMPRINT",FACE,{"disambiguationData":[TD([[makeQuery(id+"F0.imprint","IMPRINT",EDGE,{"derivedFrom":sQuery(id+"F0.wireOp",EDGE,"E1.left")}),-1.0]])]});
            var Q2;
            Q2=makeQuery(id+"F0.imprint","IMPRINT",FACE,{"disambiguationData":[TD([[makeQuery(id+"F0.imprint","IMPRINT",EDGE,{"derivedFrom":sQuery(id+"F0.wireOp",EDGE,"E28")}),-1.0]])]});
            var Q3;
            Q3=makeQuery(id+"F0.imprint","IMPRINT",FACE,{"disambiguationData":[TD([[makeQuery(id+"F0.imprint","IMPRINT",EDGE,{"derivedFrom":sQuery(id+"F0.wireOp",EDGE,"E12")}),-1.0]])]});
            var Q4;
            Q4=makeQuery(id+"F2.opExtrude","CAP_FACE",FACE,{"disambiguationData":[OSD([sQuery(id+"F0.wireOp",EDGE,"E12"),sQuery(id+"F0.wireOp",EDGE,"E13"),sQuery(id+"F0.wireOp",EDGE,"E14"),sQuery(id+"F0.wireOp",EDGE,"E15"),sQuery(id+"F0.wireOp",EDGE,"E17.filletArc"),sQuery(id+"F0.wireOp",EDGE,"E18.filletArc"),sQuery(id+"F0.wireOp",EDGE,"E19.filletArc"),sQuery(id+"F0.wireOp",EDGE,"E20.filletArc"),sQuery(id+"F0.wireOp",EDGE,"E25.0"),sQuery(id+"F0.wireOp",EDGE,"E25.1"),sQuery(id+"F0.wireOp",EDGE,"E25.2"),sQuery(id+"F0.wireOp",EDGE,"E25.3"),sQuery(id+"F0.wireOp",EDGE,"E25.4"),sQuery(id+"F0.wireOp",EDGE,"E25.5"),sQuery(id+"F0.wireOp",EDGE,"E25.6"),sQuery(id+"F0.wireOp",EDGE,"E25.7")])],"isStart":false});
            extrude(context, id + "F16", {"entities" : qUnion([Q0, Q1, Q2, Q3]), "endBound" : BoundingType.UP_TO_SURFACE, "depth" : 25 * mm, "endBoundEntityFace" : qUnion([Q4]), "offsetDistance" : 25 * mm});
        }
    });
